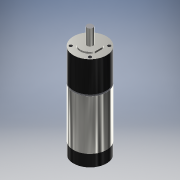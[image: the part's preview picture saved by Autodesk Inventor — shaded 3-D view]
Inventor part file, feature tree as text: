
AUTODESK INVENTOR PART (.ipt)
format: ipt  version: 2017 (Build 210142000, 142)  size: 180,224 bytes
history: native  units: mm
features: extrude x8, sketch x8, other x5, projected_geometry x1
ambient origin geometry x8: Origin, YZ Plane, XZ Plane, XY Plane, X Axis, Y Axis, Z Axis, Center Point
bodies: Body1 (feature_tree)
feature tree (22):
  other  "솔리드1"
  extrude  "돌출1"  Depth=42.4mm
  extrude  "돌출2"  Depth=39.2mm TaperAngle=0.0deg
  extrude  "돌출3"  Depth=2.0mm TaperAngle=0.0deg
  extrude  "돌출4"  Depth=42.0mm
  extrude  "돌출5"  Depth=64.0mm TaperAngle=0.0deg
  extrude  "돌출6"  Depth=15.0mm TaperAngle=0.0deg
  extrude  "돌출7"  Depth=25.0mm
  extrude  "돌출8"  Depth=2.0mm TaperAngle=0.0deg
  other  "스레드1"
  other  "스레드2"
  other  "스레드3"
  other  "스레드4"
  sketch  "스케치1"
  sketch  "스케치2"
  sketch  "스케치3"
  sketch  "스케치4"
  sketch  "스케치5"
  sketch  "스케치6"
  sketch  "스케치7"
  sketch  "스케치8"
  projected_geometry  "투영된 루프1"
